# Revit family: P191568KX-089c_KXD4636Y
name_source: partatom
category: Specialty Equipment
units: mm (PartAtom-declared; Revit-internal decimal feet)

## family parameters
Always vertical = Yes
Cut with Voids When Loaded = No
Enable Cutting in Views = No
Maintain Annotation Orientation = No
Part Type = Normal
Room Calculation Point = No
Round Connector Dimension = Use Diameter
Shared = No
Work Plane-Based = No

## types (1)
- KXD4636YSS
    Accent Material = ARCAT - Metal - Steel - Gray
    Amps = 15 A
    Body Material = ARCAT - Metal - Steel - Stainless
    Default Elevation = 0"
    Depth = 12 1/8"
    Description = 36" Retractable Downdraft System, 600 CFM
Système de ventilation escamotable à évacuation descendante de 36 po, 600 pi cu/min
    Dimension Guide = http://access.whirlpool.com Guide&sku=KXD4636YSS&language=EN
http://access.whirlpool.com Guide&sku=KXD4636YSS&language=EN
    Family Name = COOKING
    Feature 1 = Optional Interchangeable Trim Covers
Garnitures interchangeables facultatives
    Feature 2 = Auto On Function
Mise en marche automatique
    Feature 3 = 14" Rise
S’élève à 14 po
    Height = 28 1/2"
    Installation-Fabrication = http://access.whirlpool.com Instruction&sku=KXD4636YSS&language=EN
http://access.whirlpool.com Instruction&sku=KXD4636YSS&language=FR
    Manufacturer = KitchenAid
    Model = KXD4636YSS
    Voltage = 120 V
    Width = 33"

## geometry (parser evidence)
native form markers: Sweep x5
no freeform markers — native parametric forms only
